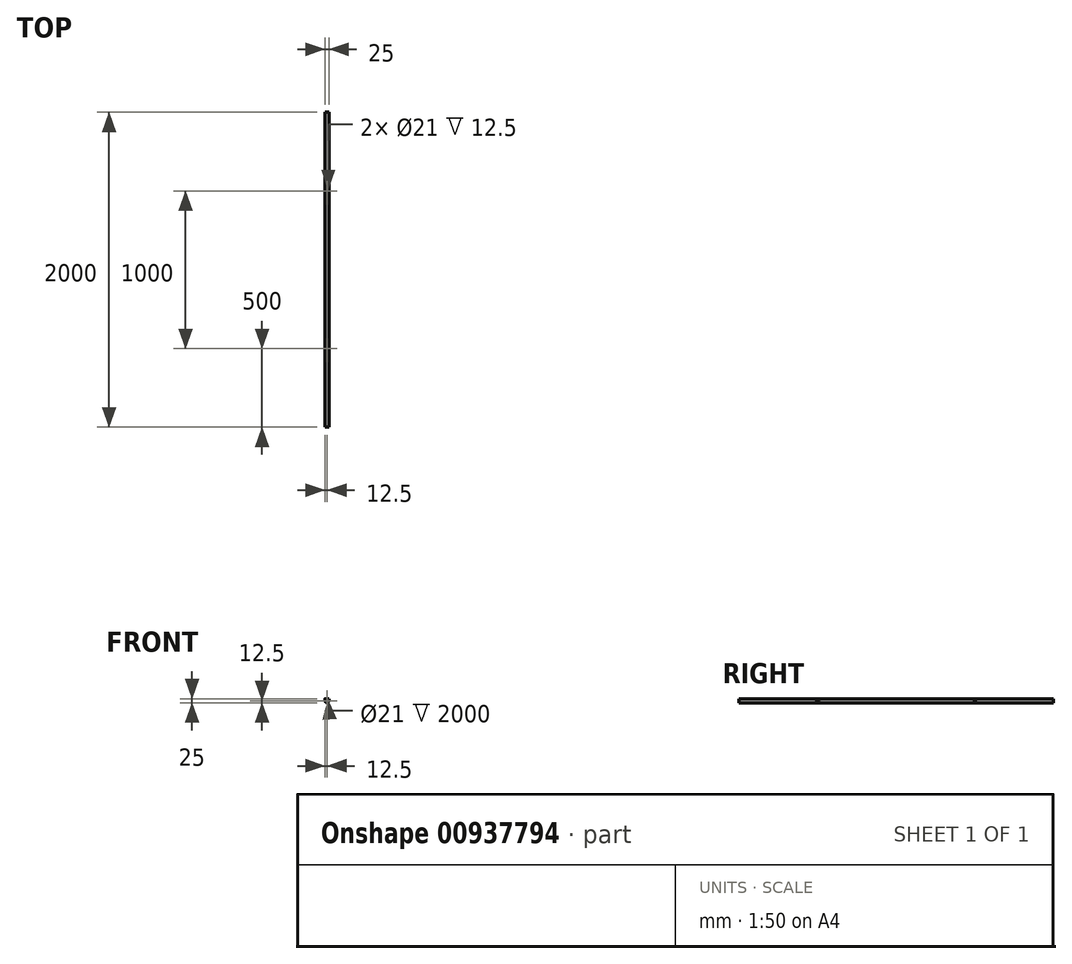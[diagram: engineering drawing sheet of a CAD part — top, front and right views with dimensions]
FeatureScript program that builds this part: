
annotation { "Feature Type Name" : "Feature", "Feature Type Description" : "" }
export const myFeature = defineFeature(function(context is Context, id is Id, definition is map)
    precondition{}
    {
        {
            var Q0;
            Q0=qCreatedBy(makeId("Front.planeOp"),FACE);
            var sketch = newSketch(context, id + "F0", { "sketchPlane" : qUnion([Q0])});
            skCircle(sketch, "E0", {"center": v(0, 0) * mm, "radius": 12.5 * mm});
            skSolve(sketch);
        }
        {
            var Q0;
            Q0=qSketchRegion(id+"F0",true);
            extrude(context, id + "F1", {"entities" : qUnion([Q0]), "depth" : 2000 * mm, "offsetDistance" : 25 * mm});
        }
        {
            var Q0;
            Q0=makeQuery(id+"F1.opExtrude","CAP_FACE",FACE,{"disambiguationData":[OSD([sQuery(id+"F0.wireOp",EDGE,"E0")])],"isStart":false});
            var sketch = newSketch(context, id + "F2", { "sketchPlane" : qUnion([Q0])});
            skCircle(sketch, "E1", {"center": v(0, 0) * mm, "radius": 10.5 * mm});
            skSolve(sketch);
        }
        {
            var Q0;
            Q0=qSketchRegion(id+"F2",true);
            extrude(context, id + "F3", {"entities" : qUnion([Q0]), "operationType" : NewBodyOperationType.REMOVE, "oppositeDirection" : true, "depth" : 2000 * mm, "offsetDistance" : 25 * mm});
        }
        {
            var Q0;
            Q0=qCreatedBy(makeId("Top.planeOp"),FACE);
            var sketch = newSketch(context, id + "F4", { "sketchPlane" : qUnion([Q0])});
            skCircle(sketch, "E2", {"center": v(0, -500) * mm, "radius": 12.5 * mm});
            skSolve(sketch);
        }
        {
            var Q0;
            Q0=qSketchRegion(id+"F4",true);
            extrude(context, id + "F5", {"entities" : qUnion([Q0]), "operationType" : NewBodyOperationType.ADD, "depth" : 12.5 * mm, "offsetDistance" : 25 * mm});
        }
        {
            var Q0;
            Q0=qCreatedBy(makeId("Front.planeOp"),FACE);
            var sketch = newSketch(context, id + "F6", { "sketchPlane" : qUnion([Q0])});
            skCircle(sketch, "E3", {"center": v(0, 0) * mm, "radius": 10.5 * mm});
            skSolve(sketch);
        }
        {
            var Q0;
            Q0=qSketchRegion(id+"F6",true);
            extrude(context, id + "F7", {"entities" : qUnion([Q0]), "operationType" : NewBodyOperationType.REMOVE, "depth" : 1000 * mm, "offsetDistance" : 25 * mm});
        }
        {
            var Q0;
            Q0=makeQuery(id+"F5.opExtrude","CAP_FACE",FACE,{"disambiguationData":[OSD([sQuery(id+"F4.wireOp",EDGE,"E2")])],"isStart":false});
            var sketch = newSketch(context, id + "F8", { "sketchPlane" : qUnion([Q0])});
            skCircle(sketch, "E4", {"center": v(0, -500) * mm, "radius": 10.5 * mm});
            skSolve(sketch);
        }
        {
            var Q0;
            Q0=qSketchRegion(id+"F8",true);
            extrude(context, id + "F9", {"entities" : qUnion([Q0]), "operationType" : NewBodyOperationType.REMOVE, "oppositeDirection" : true, "depth" : 12.5 * mm, "offsetDistance" : 25 * mm});
        }
        {
            var Q0;
            Q0=makeQuery(id+"F5.boolean.opBoolean","INTERSECT",EDGE,{"disambiguationData":[OD(0.0)],"derivedFrom":[makeQuery(id+"F1.opExtrude","SWEPT_FACE",FACE,{"disambiguationData":[OSD([sQuery(id+"F0.wireOp",EDGE,"E0")])]}),makeQuery(id+"F5.opExtrude","SWEPT_FACE",FACE,{"disambiguationData":[OSD([sQuery(id+"F4.wireOp",EDGE,"E2")])]})]});
            var Q1;
            Q1=makeQuery(id+"F5.boolean.opBoolean","INTERSECT",EDGE,{"disambiguationData":[OD(1.0)],"derivedFrom":[makeQuery(id+"F1.opExtrude","SWEPT_FACE",FACE,{"disambiguationData":[OSD([sQuery(id+"F0.wireOp",EDGE,"E0")])]}),makeQuery(id+"F5.opExtrude","SWEPT_FACE",FACE,{"disambiguationData":[OSD([sQuery(id+"F4.wireOp",EDGE,"E2")])]})]});
            fillet(context, id + "F10", {"entities" : qUnion([Q0, Q1]), "radius" : 5 * mm, "tangentPropagation" : true, "allowEdgeOverflow" : false});
        }
        {
            var Q0;
            Q0=qCreatedBy(makeId("Top.planeOp"),FACE);
            var sketch = newSketch(context, id + "F11", { "sketchPlane" : qUnion([Q0])});
            skCircle(sketch, "E5", {"center": v(0, -1500) * mm, "radius": 12.5 * mm});
            skSolve(sketch);
        }
        {
            var Q0;
            Q0=qSketchRegion(id+"F11",true);
            extrude(context, id + "F12", {"entities" : qUnion([Q0]), "operationType" : NewBodyOperationType.ADD, "depth" : 12.5 * mm, "offsetDistance" : 25 * mm});
        }
        {
            var Q0;
            Q0=makeQuery(id+"F12.opExtrude","CAP_FACE",FACE,{"disambiguationData":[OSD([sQuery(id+"F11.wireOp",EDGE,"E5")])],"isStart":false});
            var sketch = newSketch(context, id + "F13", { "sketchPlane" : qUnion([Q0])});
            skCircle(sketch, "E6", {"center": v(0, -1500) * mm, "radius": 10.5 * mm});
            skSolve(sketch);
        }
        {
            var Q0;
            Q0=qSketchRegion(id+"F13",true);
            extrude(context, id + "F14", {"entities" : qUnion([Q0]), "operationType" : NewBodyOperationType.REMOVE, "oppositeDirection" : true, "depth" : 12.5 * mm, "offsetDistance" : 25 * mm});
        }
        {
            var Q0;
            Q0=makeQuery(id+"F12.boolean.opBoolean","INTERSECT",EDGE,{"disambiguationData":[OD(2.0)],"derivedFrom":[makeQuery(id+"F1.opExtrude","SWEPT_FACE",FACE,{"disambiguationData":[OSD([sQuery(id+"F0.wireOp",EDGE,"E0")])]}),makeQuery(id+"F12.opExtrude","SWEPT_FACE",FACE,{"disambiguationData":[OSD([sQuery(id+"F11.wireOp",EDGE,"E5")])]})]});
            var Q1;
            Q1=makeQuery(id+"F12.boolean.opBoolean","INTERSECT",EDGE,{"disambiguationData":[OD(3.0)],"derivedFrom":[makeQuery(id+"F1.opExtrude","SWEPT_FACE",FACE,{"disambiguationData":[OSD([sQuery(id+"F0.wireOp",EDGE,"E0")])]}),makeQuery(id+"F12.opExtrude","SWEPT_FACE",FACE,{"disambiguationData":[OSD([sQuery(id+"F11.wireOp",EDGE,"E5")])]})]});
            fillet(context, id + "F15", {"entities" : qUnion([Q0, Q1]), "radius" : 5 * mm, "tangentPropagation" : true, "allowEdgeOverflow" : false});
        }
    });
